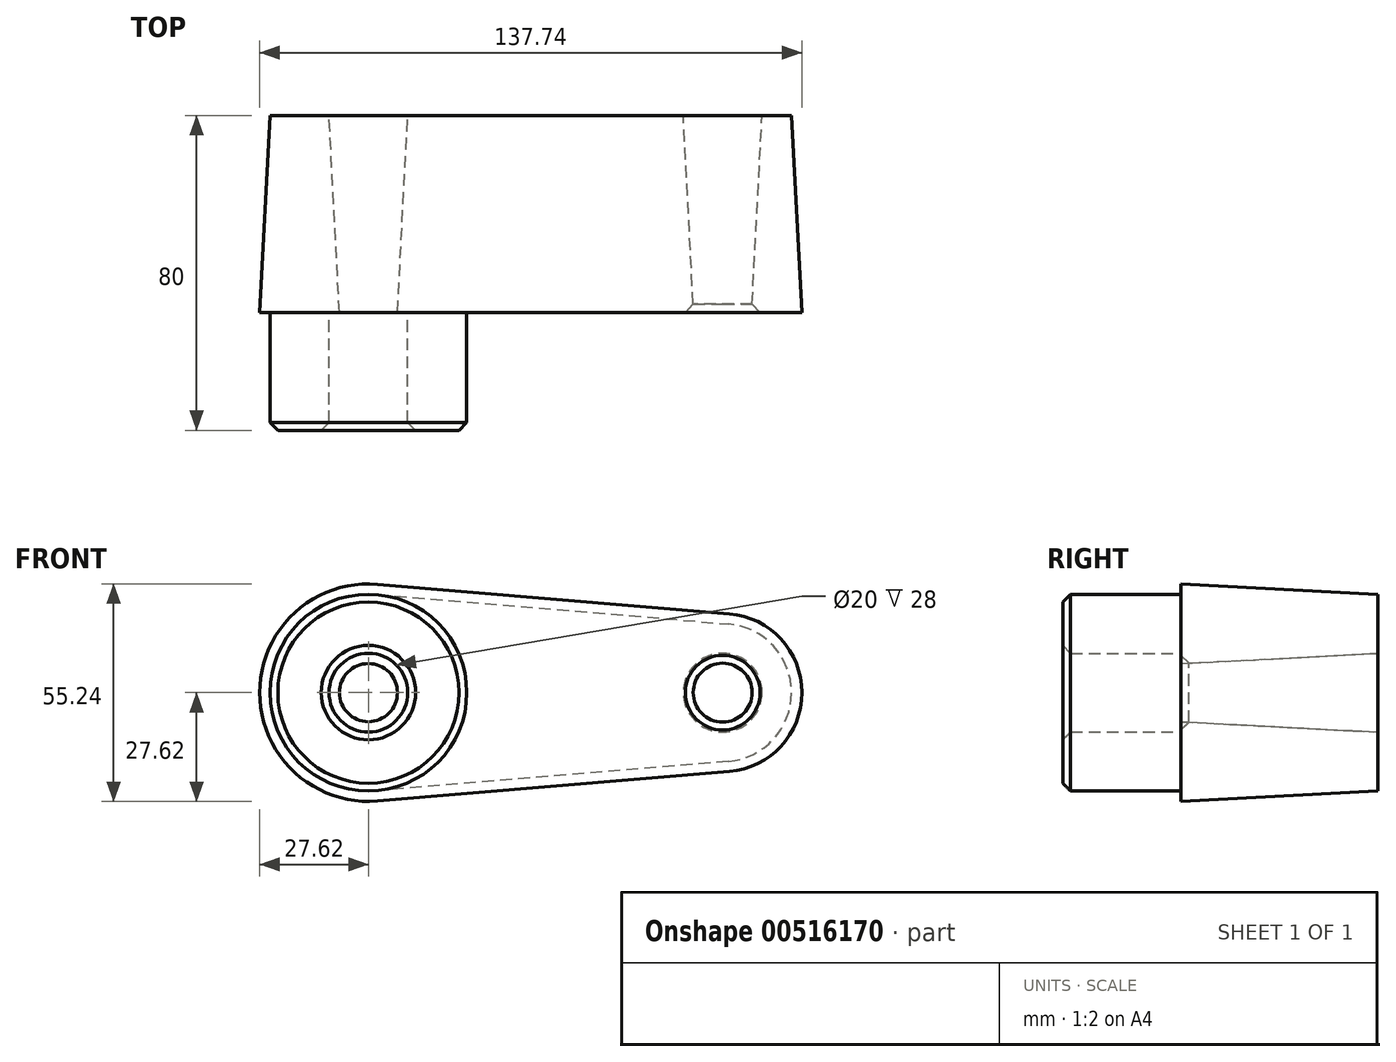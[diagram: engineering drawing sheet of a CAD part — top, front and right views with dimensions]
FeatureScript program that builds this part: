
annotation { "Feature Type Name" : "Feature", "Feature Type Description" : "" }
export const myFeature = defineFeature(function(context is Context, id is Id, definition is map)
    precondition{}
    {
        {
            var Q0;
            Q0=qCreatedBy(makeId("Front.planeOp"),FACE);
            var sketch = newSketch(context, id + "F0", { "sketchPlane" : qUnion([Q0])});
            skCircle(sketch, "E0", {"center": v(0, 0) * mm, "radius": 25 * mm});
            skCircle(sketch, "E1", {"center": v(90, 0) * mm, "radius": 17.5 * mm});
            skLineSegment(sketch, "E2", {"start": v(2.08, 24.91) * mm, "end": v(91.46, 17.44) * mm});
            skLineSegment(sketch, "E3", {"start": v(2.08, -24.91) * mm, "end": v(91.46, -17.44) * mm});
            skCircle(sketch, "E4", {"center": v(0, 0) * mm, "radius": 10 * mm});
            skCircle(sketch, "E5", {"center": v(90, 0) * mm, "radius": 10 * mm});
            skSolve(sketch);
        }
        {
            var Q0;
            Q0=qSketchRegion(id+"F0",true);
            extrude(context, id + "F1", {"entities" : qUnion([Q0]), "depth" : 50 * mm, "hasDraft" : true, "draftAngle" : 3 * degree});
        }
        {
            var Q0;
            Q0=makeQuery(id+"F0.imprint","IMPRINT",FACE,{"disambiguationData":[TD([[makeQuery(id+"F0.imprint","IMPRINT",EDGE,{"derivedFrom":sQuery(id+"F0.wireOp",EDGE,"E4")}),-1.0]])]});
            extrude(context, id + "F2", {"entities" : qUnion([Q0]), "operationType" : NewBodyOperationType.ADD, "depth" : 80 * mm});
        }
        {
            var Q0;
            Q0=makeQuery(id+"F2.opExtrude","CAP_EDGE",EDGE,{"disambiguationData":[OSD([sQuery(id+"F0.wireOp",EDGE,"E0")])],"isStart":false});
            var Q1;
            Q1=makeQuery(id+"F2.opExtrude","CAP_EDGE",EDGE,{"disambiguationData":[OSD([sQuery(id+"F0.wireOp",EDGE,"E4")])],"isStart":false});
            var Q2;
            Q2=makeQuery(id+"F1.opExtrude","CAP_EDGE",EDGE,{"disambiguationData":[OSD([sQuery(id+"F0.wireOp",EDGE,"E5")])],"isStart":false});
            chamfer(context, id + "F3", {"entities" : qUnion([Q0, Q1, Q2]), "width" : 2 * mm, "tangentPropagation" : true});
        }
    });
